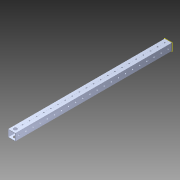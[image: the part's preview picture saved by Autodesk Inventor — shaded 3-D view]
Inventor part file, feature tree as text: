
AUTODESK INVENTOR PART (.ipt)
format: ipt  version: 2014 (Build 180170000, 170)  size: 1,319,936 bytes
history: native  units: in
note: dims shown in document units (in); Inventor stores cm internally (conversion verified against a paired STEP export)
features: extrude x4, sketch x4, pattern_circular x1, other x1, plane x1, imported_body x1
ambient origin geometry x8: Origin, YZ Plane, XZ Plane, XY Plane, X Axis, Y Axis, Z Axis, Center Point
bodies: Body1 (feature_tree)
feature tree (12):
  pattern_circular  "CirPattern2"
  other  "217-3426-STEP1"
  plane  "Work Plane1"
  extrude  "Extrusion1"  Depth=3937.0079in TaperAngle=0.0deg
  extrude  "Extrusion2"  Depth=0.5in TaperAngle=0.0deg
  extrude  "Extrusion4"  Depth=0.5in
  extrude  "Extrusion5"  Depth=0.5in
  imported_body  "Base1"
  sketch  "Sketch1"  dims[d0=-22.0in d1=3937.0079in d2=0.0in]
  sketch  "Sketch3"  dims[d3=0.5in d4=3.937in d5=0.0in]
  sketch  "Sketch5"  dims[d8=3.937in d9=0.0in d11=0.5in]
  sketch  "Sketch6"  dims[d13=8.44in d14=0.5in d15=3.937in d16=0.0in]
